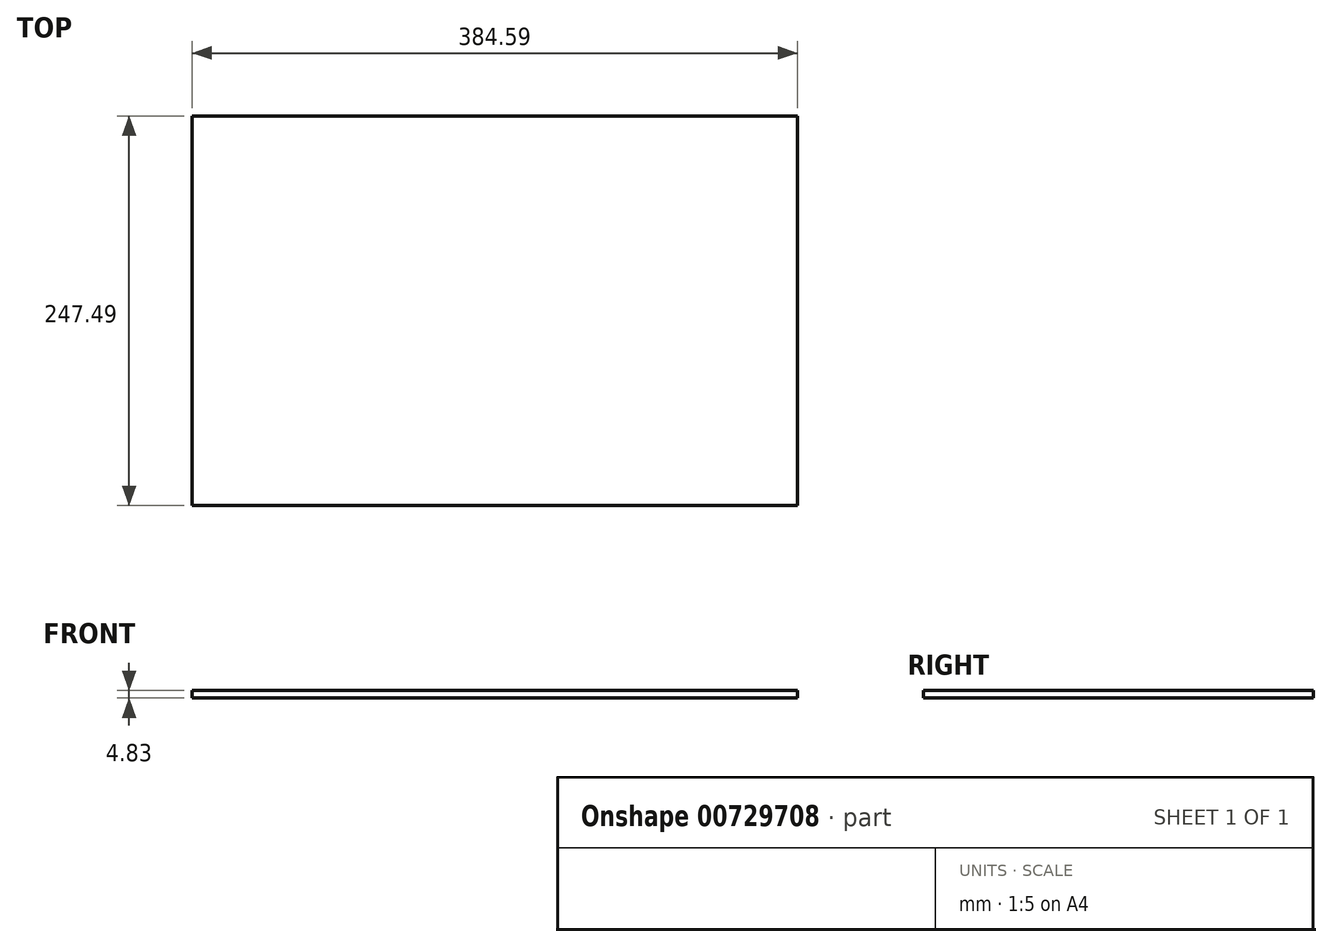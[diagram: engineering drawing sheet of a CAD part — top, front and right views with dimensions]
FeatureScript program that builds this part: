
annotation { "Feature Type Name" : "Feature", "Feature Type Description" : "" }
export const myFeature = defineFeature(function(context is Context, id is Id, definition is map)
    precondition{}
    {
        {
            var Q0;
            Q0=qCreatedBy(makeId("Top.planeOp"),FACE);
            var sketch = newSketch(context, id + "F0", { "sketchPlane" : qUnion([Q0])});
            skLineSegment(sketch, "E0.bottom", {"start": v(169.02, -127.78) * mm, "end": v(-215.57, -127.78) * mm});
            skLineSegment(sketch, "E0.top", {"start": v(169.02, 119.7) * mm, "end": v(-215.57, 119.7) * mm});
            skLineSegment(sketch, "E0.left", {"start": v(169.02, -127.78) * mm, "end": v(169.02, 119.7) * mm});
            skLineSegment(sketch, "E0.right", {"start": v(-215.57, -127.78) * mm, "end": v(-215.57, 119.7) * mm});
            skSolve(sketch);
        }
        {
            var Q0;
            Q0 = qSketchRegion(id + "F0", true);
            extrude(context, id + "F1", {"entities" : qUnion([Q0]), "depth" : 4.83 * mm, "offsetDistance" : 25.4 * mm});
        }
    });
